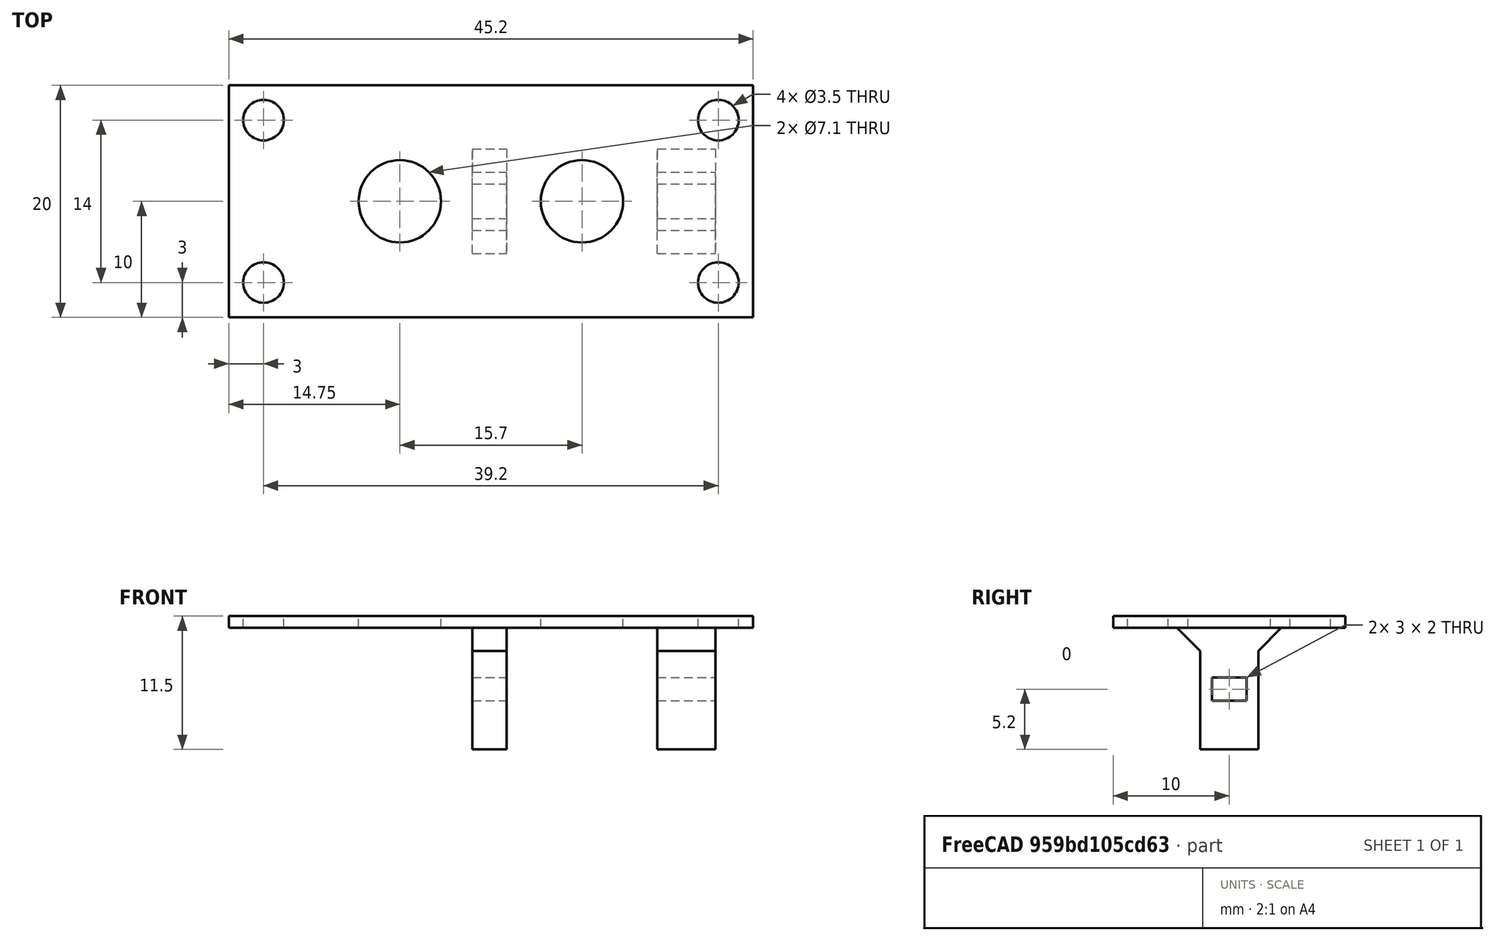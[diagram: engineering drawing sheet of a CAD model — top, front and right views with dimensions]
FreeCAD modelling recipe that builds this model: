
FCSTD DOCUMENT  (FreeCAD 0.17R13522 (Git))
Label: base2_media_con_soportes_v4
License: CreativeCommons Attribution-ShareAlike
LicenseURL: http://creativecommons.org/licenses/by-sa/4.0/
objects: Part::Cut×11, Part::Box×6, Part::Feature×6, Part::Cylinder×4, Part::Fuse×4, Part::Chamfer×3
note: 34 computed .brp shape members not serialized (recipe doc carries the construction recipe); baked Part::Feature solids carry a one-line shape summary decoded from their .brp

FEATURE [Part::Box] Box  label="base"
  AttacherType = Attacher::AttachEngine3D
  Height = 2
  Length = 45.2
  Width = 20
FEATURE [Part::Cylinder] Cylinder  label="cortador izquierda"
  Angle = 360
  AttacherType = Attacher::AttachEngine3D
  Height = 60
  Placement = pos=(14.75,10,-12) rot=(0,0,1;0rad)
  Radius = 3.55
FEATURE [Part::Feature] Cylinder001  label="cortador derecha"
  Placement = pos=(30.45,10,-4) rot=(0,0,1;0rad)
  shape: bbox 7.1 x 7.1 x 10 mm, 3 faces (baked)
FEATURE [Part::Cylinder] Cylinder002  label="sacabocado_abajo_izq"
  Angle = 360
  AttacherType = Attacher::AttachEngine3D
  Height = 10
  Placement = pos=(3,3,-4) rot=(0,0,1;0rad)
  Radius = 1.75
FEATURE [Part::Feature] Cylinder002001  label="sacabocado_abajo_derecha"
  Placement = pos=(42.2,3,-4) rot=(0,0,1;0rad)
  shape: bbox 3.5 x 3.5 x 10 mm, 3 faces (baked)
FEATURE [Part::Feature] Cylinder002002  label="sacabocado_arriba_izq"
  Placement = pos=(3,17,-4) rot=(0,0,1;0rad)
  shape: bbox 3.5 x 3.5 x 10 mm, 3 faces (baked)
FEATURE [Part::Feature] Cylinder002002001  label="sacabocado_arriba_derecha"
  Placement = pos=(42.2,17,-4) rot=(0,0,1;0rad)
  shape: bbox 3.5 x 3.5 x 10 mm, 3 faces (baked)
FEATURE [Part::Cylinder] Cylinder002002002  label="cilindro interior"
  Angle = 360
  AttacherType = Attacher::AttachEngine3D
  Height = 38.5
  Placement = pos=(14.75,10,0) rot=(0,0,1;0rad)
  Radius = 4.5
FEATURE [Part::Cylinder] Cylinder002002003  label="base cilindrica grande"
  Angle = 360
  AttacherType = Attacher::AttachEngine3D
  Height = 8.5
  Placement = pos=(14.75,10,0) rot=(0,0,1;0rad)
  Radius = 7
FEATURE [Part::Cut] Cut
  Base = -> Box
  Refine = true
  Tool = -> Cylinder002
FEATURE [Part::Cut] Cut001
  Base = -> Cut
  Refine = true
  Tool = -> Cylinder002001
FEATURE [Part::Cut] Cut002
  Base = -> Cut001
  Refine = true
  Tool = -> Cylinder001
FEATURE [Part::Cut] Cut003
  Base = -> Cut002
  Refine = true
  Tool = -> Cylinder002002001
FEATURE [Part::Cut] Cut004
  Base = -> Cut003
  Refine = true
  Tool = -> Cylinder002002
FEATURE [Part::Fuse] Fusion
  Base = -> Cylinder002002003
  Refine = true
  Tool = -> Cut004
FEATURE [Part::Fuse] Fusion001
  Base = -> Cylinder002002002
  Refine = true
  Tool = -> Fusion
FEATURE [Part::Cut] Cut005  label="pieza sin soportes"
  Base = -> Fusion001
  Refine = true
  Tool = -> Cylinder
FEATURE [Part::Box] Box001  label="soporte1"
  AttacherType = Attacher::AttachEngine3D
  Height = 10.5
  Length = 5
  Placement = pos=(36.95,7.5,-10.5) rot=(0,0,1;0rad)
  Width = 5
FEATURE [Part::Feature] Box001001  label="soporte2"
  Placement = pos=(18.95,7.5,-10.5) rot=(0,0,1;0rad)
  shape: bbox 5 x 5 x 10.5 mm, 6 faces (baked)
FEATURE [Part::Box] Box001002  label="perforador chavetas"
  AttacherType = Attacher::AttachEngine3D
  Height = 2
  Length = 30
  Placement = pos=(16,8.5,-6.3) rot=(0,0,1;0rad)
  Width = 3
FEATURE [Part::Feature] Box001002001  label="perforador chavetas001"
  Placement = pos=(16,8.5,-6.3) rot=(0,0,1;0rad)
  shape: bbox 30 x 3 x 2 mm, 6 faces (baked)
FEATURE [Part::Cut] Cut006
  Base = -> Box001
  Refine = true
  Tool = -> Box001002
FEATURE [Part::Cut] Cut007
  Base = -> Box001001
  Refine = true
  Tool = -> Box001002001
FEATURE [Part::Fuse] Fusion002
  Base = -> Cut005
  Refine = true
  Tool = -> Cut007
FEATURE [Part::Fuse] Fusion003
  Base = -> Cut006
  Refine = true
  Tool = -> Fusion002
FEATURE [Part::Chamfer] Chamfer
  Base = -> Fusion003
  Edges = 1 edges r=2: [Edge29]
FEATURE [Part::Chamfer] Chamfer001
  Base = -> Chamfer
  Edges = 1 edges r=2: [Edge19]
FEATURE [Part::Chamfer] Chamfer002  label="pieza completa"
  Base = -> Chamfer001
  Edges = 2 edges r=2: [Edge4,Edge10]
FEATURE [Part::Box] Box001002002  label="cortador separa pieza 2"
  AttacherType = Attacher::AttachEngine3D
  Height = 26
  Length = 58
  Placement = pos=(-10.65,-6,1) rot=(0,0,1;0rad)
  Width = 30
FEATURE [Part::Box] Box001002004  label="Cube"
  AttacherType = Attacher::AttachEngine3D
  Height = 30
  Length = 30
  Placement = pos=(0,0,18) rot=(0,0,1;0rad)
  Width = 30
FEATURE [Part::Cut] Cut008
  Base = -> Chamfer002
  Refine = true
  Tool = -> Box001002004
FEATURE [Part::Cut] Cut009
  Base = -> Cut008
  Refine = true
  Tool = -> Box001002002
FEATURE [Part::Box] Box001002005  label="Cube001"
  AttacherType = Attacher::AttachEngine3D
  Height = 17
  Length = 9
  Placement = pos=(12,0,-17) rot=(0,0,1;0rad)
  Width = 20
FEATURE [Part::Cut] Cut010
  Base = -> Cut009
  Refine = true
  Tool = -> Box001002005
